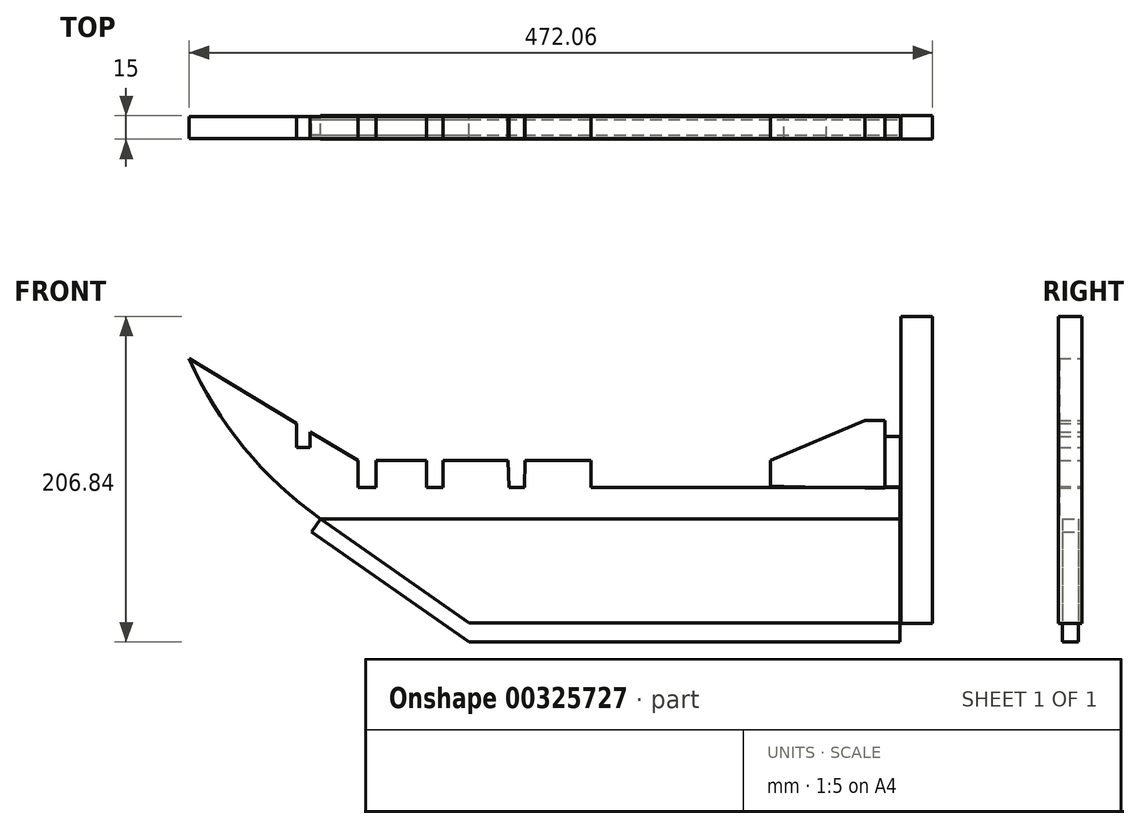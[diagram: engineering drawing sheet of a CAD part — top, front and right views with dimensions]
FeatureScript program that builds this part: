
annotation { "Feature Type Name" : "Feature", "Feature Type Description" : "" }
export const myFeature = defineFeature(function(context is Context, id is Id, definition is map)
    precondition{}
    {
        {
            var Q0;
            Q0=qCreatedBy(makeId("Front.planeOp"),FACE);
            var sketch = newSketch(context, id + "F0", { "sketchPlane" : qUnion([Q0])});
            skLineSegment(sketch, "E0.bottom", {"start": v(149.94, 137.25) * mm, "end": v(169.94, 137.25) * mm});
            skLineSegment(sketch, "E0.top", {"start": v(149.94, -57.75) * mm, "end": v(169.94, -57.75) * mm});
            skLineSegment(sketch, "E0.left", {"start": v(149.94, 137.25) * mm, "end": v(149.94, -57.75) * mm});
            skLineSegment(sketch, "E0.right", {"start": v(169.94, 137.25) * mm, "end": v(169.94, -57.75) * mm});
            skPoint(sketch, "E0.middle", {"position": v(159.94, 39.75) * mm});
            skLineSegment(sketch, "E1.bottom", {"start": v(-124.38, 8.62) * mm, "end": v(149.36, 8.62) * mm});
            skLineSegment(sketch, "E1.top", {"start": v(-124.38, -57.38) * mm, "end": v(149.36, -57.38) * mm});
            skLineSegment(sketch, "E1.left", {"start": v(-124.38, 8.62) * mm, "end": v(-124.38, -57.38) * mm});
            skLineSegment(sketch, "E1.right", {"start": v(149.36, 8.62) * mm, "end": v(149.36, -57.38) * mm});
            skPoint(sketch, "E1.middle", {"position": v(12.49, -24.38) * mm});
            skLineSegment(sketch, "E2", {"start": v(-124.38, 8.62) * mm, "end": v(-218.64, 8.62) * mm});
            skLineSegment(sketch, "E3", {"start": v(-218.64, 8.62) * mm, "end": v(-124.38, -57.38) * mm});
            skArc(sketch, "E4", {"start": v(-218.64, 8.62) * mm, "mid": v(-277.1, 66.45) * mm, "end": v(-313.05, 140.41) * mm});
            skArc(sketch, "E5.0", {"start": v(-224.38, 0.42) * mm, "mid": v(-285.23, 60.63) * mm, "end": v(-322.65, 137.62) * mm});
            skLineSegment(sketch, "E6", {"start": v(-224.38, 0.42) * mm, "end": v(-124.38, -69.6) * mm});
            skLineSegment(sketch, "E7", {"start": v(-124.38, -69.6) * mm, "end": v(169.94, -69.6) * mm});
            skLineSegment(sketch, "E8", {"start": v(169.94, -69.6) * mm, "end": v(169.94, -57.75) * mm});
            skLineSegment(sketch, "E9", {"start": v(-322.65, 137.62) * mm, "end": v(-313.05, 140.41) * mm});
            skLineSegment(sketch, "E10", {"start": v(-218.64, 8.62) * mm, "end": v(-224.38, 0.42) * mm});
            skLineSegment(sketch, "E11", {"start": v(-124.38, -57.38) * mm, "end": v(-124.38, -69.6) * mm});
            skLineSegment(sketch, "E12", {"start": v(-124.38, 8.62) * mm, "end": v(-124.38, -69.6) * mm});
            skLineSegment(sketch, "E13", {"start": v(169.94, 137.25) * mm, "end": v(169.94, -69.6) * mm});
            skLineSegment(sketch, "E14", {"start": v(149.36, 8.62) * mm, "end": v(149.36, -69.6) * mm});
            skLineSegment(sketch, "E15", {"start": v(169.94, -69.6) * mm, "end": v(149.36, -69.6) * mm});
            skLineSegment(sketch, "E16", {"start": v(169.94, -57.75) * mm, "end": v(169.94, -69.6) * mm});
            skLineSegment(sketch, "E17.bottom", {"start": v(169.94, -69.6) * mm, "end": v(149.94, -69.6) * mm});
            skLineSegment(sketch, "E17.top", {"start": v(169.94, -58.97) * mm, "end": v(149.94, -58.97) * mm});
            skLineSegment(sketch, "E17.left", {"start": v(169.94, -69.6) * mm, "end": v(169.94, -58.97) * mm});
            skLineSegment(sketch, "E17.right", {"start": v(149.94, -69.6) * mm, "end": v(149.94, -58.97) * mm});
            skPoint(sketch, "E17.middle", {"position": v(159.94, -64.28) * mm});
            skPoint(sketch, "E17.middle.positionSnap0", {"position": v(159.94, -57.75) * mm});
            skPoint(sketch, "E17.centerSnap0", {"position": v(159.94, -57.75) * mm});
            skLineSegment(sketch, "E18", {"start": v(-218.64, 8.62) * mm, "end": v(149.36, 8.62) * mm});
            skPoint(sketch, "E19", {"position": v(-34.64, 8.62) * mm});
            skLineSegment(sketch, "E20.bottom", {"start": v(149.36, 8.62) * mm, "end": v(-218.64, 8.62) * mm});
            skLineSegment(sketch, "E20.top", {"start": v(149.36, 28.55) * mm, "end": v(-218.64, 28.55) * mm});
            skLineSegment(sketch, "E20.left", {"start": v(149.36, 8.62) * mm, "end": v(149.36, 28.55) * mm});
            skLineSegment(sketch, "E20.right", {"start": v(-218.64, 8.62) * mm, "end": v(-218.64, 28.55) * mm});
            skPoint(sketch, "E20.middle", {"position": v(-34.64, 18.58) * mm});
            skLineSegment(sketch, "E21", {"start": v(-218.64, 28.55) * mm, "end": v(-243.5, 28.55) * mm});
            skLineSegment(sketch, "E22.bottom", {"start": v(139.62, 61.05) * mm, "end": v(149.62, 61.05) * mm});
            skLineSegment(sketch, "E22.top", {"start": v(139.62, 28.83) * mm, "end": v(149.62, 28.83) * mm});
            skLineSegment(sketch, "E22.left", {"start": v(139.62, 61.05) * mm, "end": v(139.62, 28.83) * mm});
            skLineSegment(sketch, "E22.right", {"start": v(149.62, 61.05) * mm, "end": v(149.62, 28.83) * mm});
            skPoint(sketch, "E22.middle", {"position": v(144.62, 44.94) * mm});
            skLineSegment(sketch, "E23.bottom", {"start": v(126.9, 71.05) * mm, "end": v(139.78, 71.05) * mm});
            skLineSegment(sketch, "E23.top", {"start": v(126.9, 28.1) * mm, "end": v(139.78, 28.1) * mm});
            skLineSegment(sketch, "E23.left", {"start": v(126.9, 71.05) * mm, "end": v(126.9, 28.1) * mm});
            skLineSegment(sketch, "E23.right", {"start": v(139.78, 71.05) * mm, "end": v(139.78, 28.1) * mm});
            skPoint(sketch, "E23.middle", {"position": v(133.34, 49.57) * mm});
            skLineSegment(sketch, "E24.bottom", {"start": v(75.43, 45.58) * mm, "end": v(66.9, 45.58) * mm});
            skLineSegment(sketch, "E24.top", {"start": v(75.43, 29.08) * mm, "end": v(66.9, 29.08) * mm});
            skLineSegment(sketch, "E24.left", {"start": v(75.43, 45.58) * mm, "end": v(75.43, 29.08) * mm});
            skLineSegment(sketch, "E24.right", {"start": v(66.9, 45.58) * mm, "end": v(66.9, 29.08) * mm});
            skPoint(sketch, "E24.middle", {"position": v(71.16, 37.33) * mm});
            skLineSegment(sketch, "E25", {"start": v(66.9, 45.58) * mm, "end": v(126.9, 71.05) * mm});
            skLineSegment(sketch, "E26.bottom", {"start": v(56.9, 28.55) * mm, "end": v(14.9, 28.55) * mm});
            skLineSegment(sketch, "E27.bottom", {"start": v(4.9, 28.55) * mm, "end": v(-37.1, 28.55) * mm});
            skPoint(sketch, "E28", {"position": v(-47.1, 28.55) * mm});
            skPoint(sketch, "E29", {"position": v(-89.1, 28.55) * mm});
            skPoint(sketch, "E30", {"position": v(-302.12, 110.35) * mm});
            skPoint(sketch, "E31", {"position": v(-99.1, 28.55) * mm});
            skPoint(sketch, "E32", {"position": v(-141.1, 28.55) * mm});
            skPoint(sketch, "E33", {"position": v(-151.6, 28.55) * mm});
            skPoint(sketch, "E34", {"position": v(66.9, 45.58) * mm});
            skPoint(sketch, "E35", {"position": v(126.9, 71.05) * mm});
            skPoint(sketch, "E36", {"position": v(126.9, 28.1) * mm});
            skPoint(sketch, "E37", {"position": v(75.43, 29.08) * mm});
            skLineSegment(sketch, "E38", {"start": v(75.43, 29.08) * mm, "end": v(126.9, 28.1) * mm});
            skPoint(sketch, "E39", {"position": v(56.9, 45.58) * mm});
            skPoint(sketch, "E40", {"position": v(14.97, 45.58) * mm});
            skPoint(sketch, "E41", {"position": v(4.91, 45.58) * mm});
            skPoint(sketch, "E42", {"position": v(-36.93, 45.58) * mm});
            skPoint(sketch, "E43", {"position": v(-46.99, 45.58) * mm});
            skPoint(sketch, "E44", {"position": v(-88.83, 45.58) * mm});
            skPoint(sketch, "E45", {"position": v(-99.7, 45.58) * mm});
            skPoint(sketch, "E46", {"position": v(-141.13, 45.58) * mm});
            skPoint(sketch, "E47", {"position": v(-151.6, 45.58) * mm});
            skPoint(sketch, "E48", {"position": v(-183.38, 45.58) * mm});
            skLineSegment(sketch, "E49", {"start": v(56.9, 45.58) * mm, "end": v(56.9, 28.55) * mm});
            skLineSegment(sketch, "E50", {"start": v(56.9, 45.58) * mm, "end": v(14.97, 45.58) * mm});
            skLineSegment(sketch, "E51", {"start": v(14.9, 28.55) * mm, "end": v(14.97, 45.58) * mm});
            skLineSegment(sketch, "E52", {"start": v(4.91, 45.58) * mm, "end": v(4.9, 28.55) * mm});
            skLineSegment(sketch, "E53", {"start": v(-37.1, 28.55) * mm, "end": v(-36.93, 45.58) * mm});
            skLineSegment(sketch, "E54", {"start": v(-36.93, 45.58) * mm, "end": v(4.91, 45.58) * mm});
            skLineSegment(sketch, "E55", {"start": v(-46.99, 45.58) * mm, "end": v(-47.1, 28.55) * mm});
            skLineSegment(sketch, "E56", {"start": v(-89.1, 28.55) * mm, "end": v(-88.83, 45.58) * mm});
            skLineSegment(sketch, "E57", {"start": v(-88.83, 45.58) * mm, "end": v(-46.99, 45.58) * mm});
            skLineSegment(sketch, "E58", {"start": v(-99.7, 45.58) * mm, "end": v(-99.1, 28.55) * mm});
            skLineSegment(sketch, "E59", {"start": v(-141.1, 28.55) * mm, "end": v(-141.13, 45.58) * mm});
            skLineSegment(sketch, "E60", {"start": v(-99.7, 45.58) * mm, "end": v(-141.13, 45.58) * mm});
            skPoint(sketch, "E61", {"position": v(-183.38, 28.55) * mm});
            skLineSegment(sketch, "E62", {"start": v(-151.6, 45.58) * mm, "end": v(-151.6, 28.55) * mm});
            skLineSegment(sketch, "E63", {"start": v(-183.38, 45.58) * mm, "end": v(-183.38, 28.55) * mm});
            skLineSegment(sketch, "E64", {"start": v(-183.38, 45.58) * mm, "end": v(-151.6, 45.58) * mm});
            skPoint(sketch, "E65", {"position": v(-225.38, 109.12) * mm});
            skLineSegment(sketch, "E66", {"start": v(-225.38, 109.12) * mm, "end": v(-225.38, 28.55) * mm, "construction": true});
            skPoint(sketch, "E67", {"position": v(-195.1, 45.58) * mm});
            skPoint(sketch, "E68", {"position": v(-195.1, 28.55) * mm});
            skLineSegment(sketch, "E69", {"start": v(-195.1, 45.58) * mm, "end": v(-195.1, 28.55) * mm});
            skLineSegment(sketch, "E70", {"start": v(-302.12, 110.35) * mm, "end": v(-195.1, 45.58) * mm, "construction": true});
            skPoint(sketch, "E71", {"position": v(-225.38, 63.9) * mm});
            skPoint(sketch, "E72", {"position": v(-233.93, 69.08) * mm});
            skLineSegment(sketch, "E73", {"start": v(-225.38, 63.9) * mm, "end": v(-195.1, 45.58) * mm});
            skLineSegment(sketch, "E74", {"start": v(-233.93, 69.08) * mm, "end": v(-302.12, 110.35) * mm});
            skLineSegment(sketch, "E75", {"start": v(-195.1, 28.55) * mm, "end": v(-243.5, 28.55) * mm});
            skPoint(sketch, "E76", {"position": v(-225.38, 53.9) * mm});
            skPoint(sketch, "E77", {"position": v(-233.93, 53.9) * mm});
            skLineSegment(sketch, "E78", {"start": v(-225.38, 63.9) * mm, "end": v(-225.38, 53.9) * mm});
            skLineSegment(sketch, "E79", {"start": v(-233.93, 69.08) * mm, "end": v(-233.93, 53.9) * mm});
            skLineSegment(sketch, "E80", {"start": v(-225.38, 53.9) * mm, "end": v(-233.93, 53.9) * mm});
            skLineSegment(sketch, "E81", {"start": v(-195.1, 45.58) * mm, "end": v(-141.13, 45.58) * mm, "construction": true});
            skLineSegment(sketch, "E82", {"start": v(66.9, 45.58) * mm, "end": v(4.91, 45.58) * mm, "construction": true});
            skSolve(sketch);
        }
        {
            var Q0;
            {var subQ0=sQuery(id+"F0.wireOp",EDGE,"E3");Q0=makeQuery(id+"F0.imprint","IMPRINT",FACE,{"disambiguationData":[TD([[makeQuery(id+"F0.imprint","IMPRINT",EDGE,{"derivedFrom":subQ0}),1.0]])]});}
            var Q1;
            {var subQ0=sQuery(id+"F0.wireOp",EDGE,"E1.top");Q1=makeQuery(id+"F0.imprint","IMPRINT",FACE,{"disambiguationData":[TD([[makeQuery(id+"F0.imprint","IMPRINT",EDGE,{"derivedFrom":subQ0}),1.0]])]});}
            var Q2;
            Q2=makeQuery(id+"F0.imprint","IMPRINT",FACE,{"disambiguationData":[TD([[makeQuery(id+"F0.imprint","IMPRINT",EDGE,{"derivedFrom":sQuery(id+"F0.wireOp",EDGE,"E0.bottom")}),-1.0]])]});
            extrude(context, id + "F1", {"entities" : qUnion([Q0, Q1, Q2]), "endBound" : BoundingType.SYMMETRIC, "depth" : 15 * mm});
        }
        {
            var Q0;
            Q0=makeQuery(id+"F0.imprint","IMPRINT",FACE,{"disambiguationData":[TD([[makeQuery(id+"F0.imprint","IMPRINT",EDGE,{"derivedFrom":sQuery(id+"F0.wireOp",EDGE,"E5.0")}),-1.0]])]});
            var Q1;
            {var subQ0=sQuery(id+"F0.wireOp",EDGE,"E3");Q1=makeQuery(id+"F0.imprint","IMPRINT",FACE,{"disambiguationData":[TD([[makeQuery(id+"F0.imprint","IMPRINT",EDGE,{"derivedFrom":subQ0}),-1.0]])]});}
            var Q2;
            {var subQ0=sQuery(id+"F0.wireOp",EDGE,"E1.top");Q2=makeQuery(id+"F0.imprint","IMPRINT",FACE,{"disambiguationData":[TD([[makeQuery(id+"F0.imprint","IMPRINT",EDGE,{"derivedFrom":subQ0}),-1.0]])]});}
            var Q3;
            Q3=makeQuery(id+"F0.imprint","IMPRINT",FACE,{"disambiguationData":[TD([[makeQuery(id+"F0.imprint","IMPRINT",EDGE,{"derivedFrom":sQuery(id+"F0.wireOp",EDGE,"E17.bottom")}),-1.0]])]});
            extrude(context, id + "F2", {"entities" : qUnion([Q0, Q1, Q2, Q3]), "operationType" : NewBodyOperationType.ADD, "endBound" : BoundingType.SYMMETRIC, "depth" : 10 * mm});
        }
        {
            var Q0;
            {var subQ13=sQuery(id+"F0.wireOp",EDGE,"E20.left");Q0=makeQuery(id+"F0.imprint","IMPRINT",FACE,{"disambiguationData":[TD([[makeQuery(id+"F0.imprint","IMPRINT",EDGE,{"derivedFrom":subQ13}),1.0]])]});}
            var Q1;
            {var subQ0=sQuery(id+"F0.wireOp",EDGE,"E20.right");Q1=makeQuery(id+"F0.imprint","IMPRINT",FACE,{"disambiguationData":[TD([[makeQuery(id+"F0.imprint","IMPRINT",EDGE,{"derivedFrom":subQ0}),1.0]])]});}
            var Q2;
            {var subQ1=sQuery(id+"F0.wireOp",EDGE,"E69");Q2=makeQuery(id+"F0.imprint","IMPRINT",FACE,{"disambiguationData":[TD([[makeQuery(id+"F0.imprint","IMPRINT",EDGE,{"derivedFrom":subQ1}),-1.0]])]});}
            var Q3;
            {var subQ0=sQuery(id+"F0.wireOp",EDGE,"E62");Q3=makeQuery(id+"F0.imprint","IMPRINT",FACE,{"disambiguationData":[TD([[makeQuery(id+"F0.imprint","IMPRINT",EDGE,{"derivedFrom":subQ0}),-1.0]])]});}
            var Q4;
            {var subQ0=sQuery(id+"F0.wireOp",EDGE,"E58");Q4=makeQuery(id+"F0.imprint","IMPRINT",FACE,{"disambiguationData":[TD([[makeQuery(id+"F0.imprint","IMPRINT",EDGE,{"derivedFrom":subQ0}),-1.0]])]});}
            var Q5;
            {var subQ0=sQuery(id+"F0.wireOp",EDGE,"E55");Q5=makeQuery(id+"F0.imprint","IMPRINT",FACE,{"disambiguationData":[TD([[makeQuery(id+"F0.imprint","IMPRINT",EDGE,{"derivedFrom":subQ0}),-1.0]])]});}
            var Q6;
            Q6=makeQuery(id+"F0.imprint","IMPRINT",FACE,{"disambiguationData":[TD([[makeQuery(id+"F0.imprint","IMPRINT",EDGE,{"derivedFrom":sQuery(id+"F0.wireOp",EDGE,"E27.bottom")}),-1.0]])]});
            var Q7;
            Q7=makeQuery(id+"F0.imprint","IMPRINT",FACE,{"disambiguationData":[TD([[makeQuery(id+"F0.imprint","IMPRINT",EDGE,{"derivedFrom":sQuery(id+"F0.wireOp",EDGE,"E26.bottom")}),-1.0]])]});
            var Q8;
            Q8=makeQuery(id+"F0.imprint","IMPRINT",FACE,{"disambiguationData":[TD([[makeQuery(id+"F0.imprint","IMPRINT",EDGE,{"derivedFrom":sQuery(id+"F0.wireOp",EDGE,"E24.bottom")}),-1.0]])]});
            var Q9;
            Q9=makeQuery(id+"F0.imprint","IMPRINT",FACE,{"disambiguationData":[TD([[makeQuery(id+"F0.imprint","IMPRINT",EDGE,{"derivedFrom":sQuery(id+"F0.wireOp",EDGE,"E24.bottom")}),1.0]])]});
            var Q10;
            {var subQ0=sQuery(id+"F0.wireOp",EDGE,"E22.left");Q10=makeQuery(id+"F0.imprint","IMPRINT",FACE,{"disambiguationData":[TD([[makeQuery(id+"F0.imprint","IMPRINT",EDGE,{"derivedFrom":subQ0}),-1.0]])]});}
            var Q11;
            {var subQ0=sQuery(id+"F0.wireOp",EDGE,"E22.right");Q11=makeQuery(id+"F0.imprint","IMPRINT",FACE,{"disambiguationData":[TD([[makeQuery(id+"F0.imprint","IMPRINT",EDGE,{"derivedFrom":subQ0}),-1.0]])]});}
            extrude(context, id + "F3", {"entities" : qUnion([Q0, Q1, Q2, Q3, Q4, Q5, Q6, Q7, Q8, Q9, Q10, Q11]), "operationType" : NewBodyOperationType.ADD, "endBound" : BoundingType.SYMMETRIC, "depth" : 14 * mm});
        }
    });
